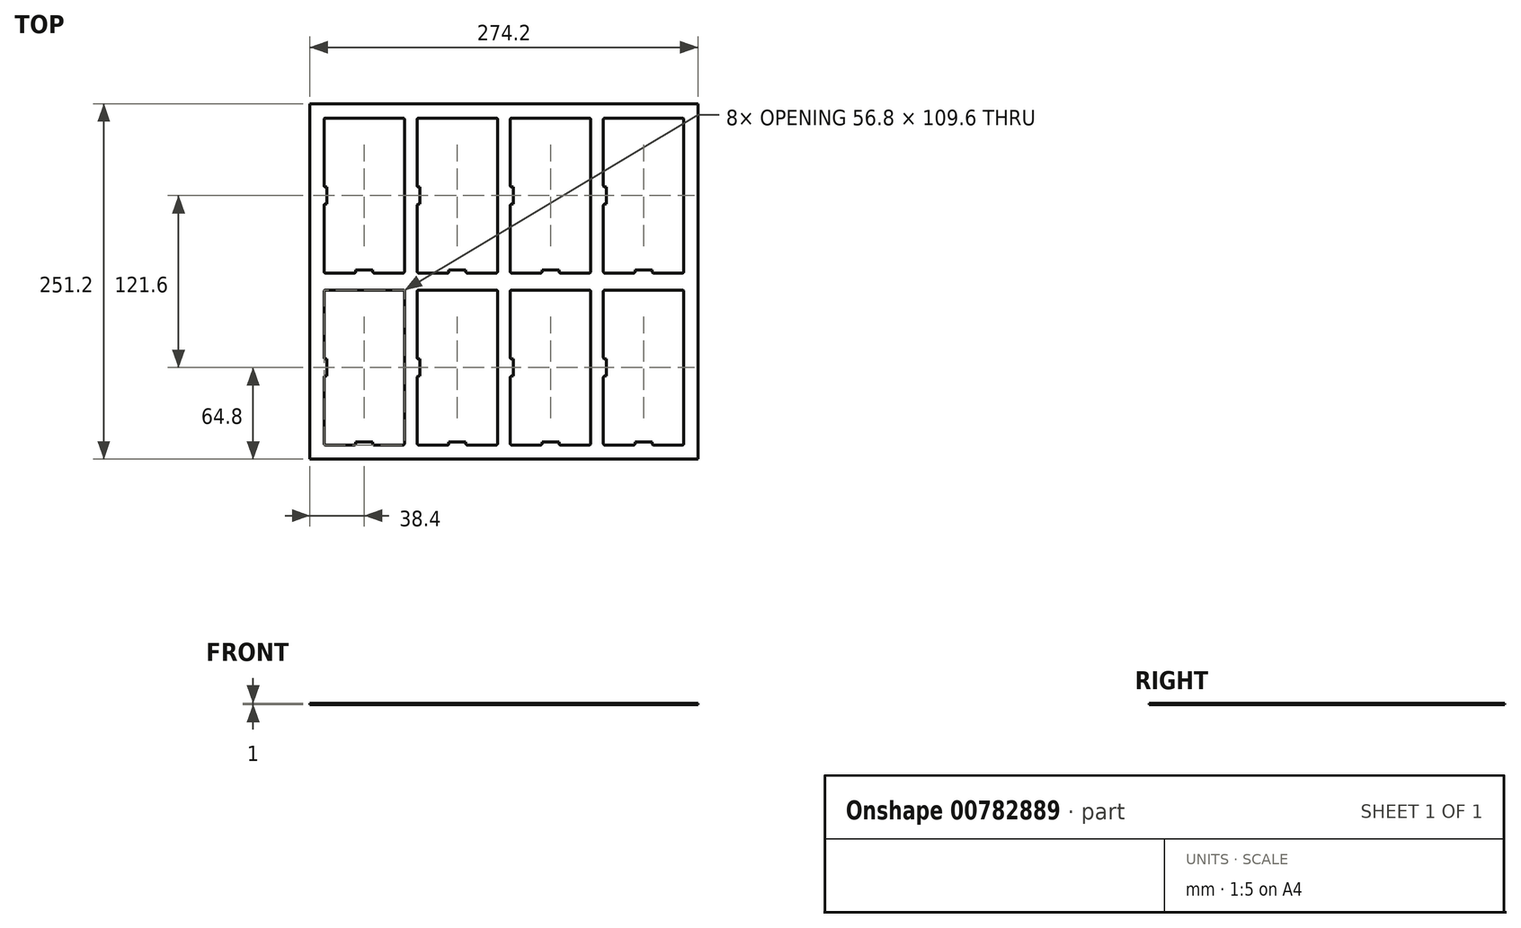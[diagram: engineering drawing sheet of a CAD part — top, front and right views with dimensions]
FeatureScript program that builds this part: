
annotation { "Feature Type Name" : "Feature", "Feature Type Description" : "" }
export const myFeature = defineFeature(function(context is Context, id is Id, definition is map)
    precondition{}
    {
        {
            var Q0;
            Q0=qCreatedBy(makeId("Top.planeOp"),FACE);
            var sketch = newSketch(context, id + "F0", { "sketchPlane" : qUnion([Q0])});
            skLineSegment(sketch, "E0.bottom", {"start": v(137.1, -125.6) * mm, "end": v(-137.1, -125.6) * mm});
            skLineSegment(sketch, "E0.top", {"start": v(137.1, 125.6) * mm, "end": v(-137.1, 125.6) * mm});
            skLineSegment(sketch, "E0.left", {"start": v(137.1, -125.6) * mm, "end": v(137.1, 125.6) * mm});
            skLineSegment(sketch, "E0.right", {"start": v(-137.1, -125.6) * mm, "end": v(-137.1, 125.6) * mm});
            skPoint(sketch, "E0.middle", {"position": v(0, 0) * mm});
            skSolve(sketch);
        }
        {
            var Q0;
            Q0 = qSketchRegion(id + "F0", true);
            extrude(context, id + "F1", {"entities" : qUnion([Q0]), "depth" : 1 * mm, "offsetDistance" : 25 * mm});
        }
        {
            var Q0;
            Q0=makeQuery(id+"F1.opExtrude","CAP_FACE",FACE,{"disambiguationData":[OSD([sQuery(id+"F0.wireOp",EDGE,"E0.bottom"),sQuery(id+"F0.wireOp",EDGE,"E0.top"),sQuery(id+"F0.wireOp",EDGE,"E0.left"),sQuery(id+"F0.wireOp",EDGE,"E0.right")])],"isStart":false});
            var sketch = newSketch(context, id + "F2", { "sketchPlane" : qUnion([Q0])});
            skLineSegment(sketch, "E1.bottom", {"start": v(-125.1, -10) * mm, "end": v(-74.3, -10) * mm, "construction": true});
            skLineSegment(sketch, "E1.top", {"start": v(-125.1, -113.6) * mm, "end": v(-74.3, -113.6) * mm, "construction": true});
            skLineSegment(sketch, "E1.left", {"start": v(-125.1, -10) * mm, "end": v(-125.1, -113.6) * mm, "construction": true});
            skLineSegment(sketch, "E1.right", {"start": v(-74.3, -10) * mm, "end": v(-74.3, -113.6) * mm, "construction": true});
            skLineSegment(sketch, "E2.bottom", {"start": v(-127.1, -115.6) * mm, "end": v(-70.3, -115.6) * mm});
            skLineSegment(sketch, "E2.top", {"start": v(-127.1, -6) * mm, "end": v(-70.3, -6) * mm});
            skLineSegment(sketch, "E2.left", {"start": v(-127.1, -115.6) * mm, "end": v(-127.1, -6) * mm});
            skLineSegment(sketch, "E2.right", {"start": v(-70.3, -115.6) * mm, "end": v(-70.3, -6) * mm});
            skLineSegment(sketch, "E3.top", {"start": v(-92.7, -113.6) * mm, "end": v(-104.7, -113.6) * mm});
            skLineSegment(sketch, "E3.left", {"start": v(-92.7, -115.6) * mm, "end": v(-92.7, -113.6) * mm});
            skLineSegment(sketch, "E3.right", {"start": v(-104.7, -115.6) * mm, "end": v(-104.7, -113.6) * mm});
            skPoint(sketch, "E3.middle", {"position": v(-98.7, -115.6) * mm});
            skPoint(sketch, "E4.orphan", {"position": v(-104.7, -117.6) * mm});
            skPoint(sketch, "E5.orphan", {"position": v(-92.7, -117.6) * mm});
            skLineSegment(sketch, "E6.bottom", {"start": v(-125.1, -66.8) * mm, "end": v(-127.1, -66.8) * mm});
            skLineSegment(sketch, "E6.top", {"start": v(-125.1, -54.8) * mm, "end": v(-127.1, -54.8) * mm});
            skLineSegment(sketch, "E6.left", {"start": v(-125.1, -66.8) * mm, "end": v(-125.1, -54.8) * mm});
            skPoint(sketch, "E6.middle", {"position": v(-127.1, -60.8) * mm});
            skPoint(sketch, "E7.orphan", {"position": v(-129.1, -54.8) * mm});
            skPoint(sketch, "E8.orphan", {"position": v(-129.1, -66.8) * mm});
            skLineSegment(sketch, "E9.0.1.0", {"start": v(-127.1, 115.6) * mm, "end": v(-70.3, 115.6) * mm});
            skLineSegment(sketch, "E9.0.1.1", {"start": v(-70.3, 6) * mm, "end": v(-70.3, 115.6) * mm});
            skLineSegment(sketch, "E9.0.1.2", {"start": v(-127.1, 6) * mm, "end": v(-70.3, 6) * mm});
            skLineSegment(sketch, "E9.0.1.3", {"start": v(-127.1, 6) * mm, "end": v(-127.1, 115.6) * mm});
            skLineSegment(sketch, "E9.0.1.4", {"start": v(-104.7, 6) * mm, "end": v(-104.7, 8) * mm});
            skLineSegment(sketch, "E9.0.1.5", {"start": v(-92.7, 6) * mm, "end": v(-92.7, 8) * mm});
            skLineSegment(sketch, "E9.0.1.6", {"start": v(-92.7, 8) * mm, "end": v(-104.7, 8) * mm});
            skLineSegment(sketch, "E9.0.1.7", {"start": v(-125.1, 66.8) * mm, "end": v(-127.1, 66.8) * mm});
            skLineSegment(sketch, "E9.0.1.8", {"start": v(-125.1, 54.8) * mm, "end": v(-127.1, 54.8) * mm});
            skLineSegment(sketch, "E9.0.1.9", {"start": v(-125.1, 54.8) * mm, "end": v(-125.1, 66.8) * mm});
            skLineSegment(sketch, "E9.1.0.0", {"start": v(-61.3, -6) * mm, "end": v(-4.5, -6) * mm});
            skLineSegment(sketch, "E9.1.0.1", {"start": v(-4.5, -115.6) * mm, "end": v(-4.5, -6) * mm});
            skLineSegment(sketch, "E9.1.0.2", {"start": v(-61.3, -115.6) * mm, "end": v(-4.5, -115.6) * mm});
            skLineSegment(sketch, "E9.1.0.3", {"start": v(-61.3, -115.6) * mm, "end": v(-61.3, -6) * mm});
            skLineSegment(sketch, "E9.1.0.4", {"start": v(-38.9, -115.6) * mm, "end": v(-38.9, -113.6) * mm});
            skLineSegment(sketch, "E9.1.0.5", {"start": v(-26.9, -115.6) * mm, "end": v(-26.9, -113.6) * mm});
            skLineSegment(sketch, "E9.1.0.6", {"start": v(-26.9, -113.6) * mm, "end": v(-38.9, -113.6) * mm});
            skLineSegment(sketch, "E9.1.0.7", {"start": v(-59.3, -54.8) * mm, "end": v(-61.3, -54.8) * mm});
            skLineSegment(sketch, "E9.1.0.8", {"start": v(-59.3, -66.8) * mm, "end": v(-61.3, -66.8) * mm});
            skLineSegment(sketch, "E9.1.0.9", {"start": v(-59.3, -66.8) * mm, "end": v(-59.3, -54.8) * mm});
            skLineSegment(sketch, "E9.1.1.0", {"start": v(-61.3, 115.6) * mm, "end": v(-4.5, 115.6) * mm});
            skLineSegment(sketch, "E9.1.1.1", {"start": v(-4.5, 6) * mm, "end": v(-4.5, 115.6) * mm});
            skLineSegment(sketch, "E9.1.1.2", {"start": v(-61.3, 6) * mm, "end": v(-4.5, 6) * mm});
            skLineSegment(sketch, "E9.1.1.3", {"start": v(-61.3, 6) * mm, "end": v(-61.3, 115.6) * mm});
            skLineSegment(sketch, "E9.1.1.4", {"start": v(-38.9, 6) * mm, "end": v(-38.9, 8) * mm});
            skLineSegment(sketch, "E9.1.1.5", {"start": v(-26.9, 6) * mm, "end": v(-26.9, 8) * mm});
            skLineSegment(sketch, "E9.1.1.6", {"start": v(-26.9, 8) * mm, "end": v(-38.9, 8) * mm});
            skLineSegment(sketch, "E9.1.1.7", {"start": v(-59.3, 66.8) * mm, "end": v(-61.3, 66.8) * mm});
            skLineSegment(sketch, "E9.1.1.8", {"start": v(-59.3, 54.8) * mm, "end": v(-61.3, 54.8) * mm});
            skLineSegment(sketch, "E9.1.1.9", {"start": v(-59.3, 54.8) * mm, "end": v(-59.3, 66.8) * mm});
            skLineSegment(sketch, "E9.2.0.0", {"start": v(4.5, -6) * mm, "end": v(61.3, -6) * mm});
            skLineSegment(sketch, "E9.2.0.1", {"start": v(61.3, -115.6) * mm, "end": v(61.3, -6) * mm});
            skLineSegment(sketch, "E9.2.0.2", {"start": v(4.5, -115.6) * mm, "end": v(61.3, -115.6) * mm});
            skLineSegment(sketch, "E9.2.0.3", {"start": v(4.5, -115.6) * mm, "end": v(4.5, -6) * mm});
            skLineSegment(sketch, "E9.2.0.4", {"start": v(26.9, -115.6) * mm, "end": v(26.9, -113.6) * mm});
            skLineSegment(sketch, "E9.2.0.5", {"start": v(38.9, -115.6) * mm, "end": v(38.9, -113.6) * mm});
            skLineSegment(sketch, "E9.2.0.6", {"start": v(38.9, -113.6) * mm, "end": v(26.9, -113.6) * mm});
            skLineSegment(sketch, "E9.2.0.7", {"start": v(6.5, -54.8) * mm, "end": v(4.5, -54.8) * mm});
            skLineSegment(sketch, "E9.2.0.8", {"start": v(6.5, -66.8) * mm, "end": v(4.5, -66.8) * mm});
            skLineSegment(sketch, "E9.2.0.9", {"start": v(6.5, -66.8) * mm, "end": v(6.5, -54.8) * mm});
            skLineSegment(sketch, "E9.2.1.0", {"start": v(4.5, 115.6) * mm, "end": v(61.3, 115.6) * mm});
            skLineSegment(sketch, "E9.2.1.1", {"start": v(61.3, 6) * mm, "end": v(61.3, 115.6) * mm});
            skLineSegment(sketch, "E9.2.1.2", {"start": v(4.5, 6) * mm, "end": v(61.3, 6) * mm});
            skLineSegment(sketch, "E9.2.1.3", {"start": v(4.5, 6) * mm, "end": v(4.5, 115.6) * mm});
            skLineSegment(sketch, "E9.2.1.4", {"start": v(26.9, 6) * mm, "end": v(26.9, 8) * mm});
            skLineSegment(sketch, "E9.2.1.5", {"start": v(38.9, 6) * mm, "end": v(38.9, 8) * mm});
            skLineSegment(sketch, "E9.2.1.6", {"start": v(38.9, 8) * mm, "end": v(26.9, 8) * mm});
            skLineSegment(sketch, "E9.2.1.7", {"start": v(6.5, 66.8) * mm, "end": v(4.5, 66.8) * mm});
            skLineSegment(sketch, "E9.2.1.8", {"start": v(6.5, 54.8) * mm, "end": v(4.5, 54.8) * mm});
            skLineSegment(sketch, "E9.2.1.9", {"start": v(6.5, 54.8) * mm, "end": v(6.5, 66.8) * mm});
            skLineSegment(sketch, "E9.3.0.0", {"start": v(70.3, -6) * mm, "end": v(127.1, -6) * mm});
            skLineSegment(sketch, "E9.3.0.1", {"start": v(127.1, -115.6) * mm, "end": v(127.1, -6) * mm});
            skLineSegment(sketch, "E9.3.0.2", {"start": v(70.3, -115.6) * mm, "end": v(127.1, -115.6) * mm});
            skLineSegment(sketch, "E9.3.0.3", {"start": v(70.3, -115.6) * mm, "end": v(70.3, -6) * mm});
            skLineSegment(sketch, "E9.3.0.4", {"start": v(92.7, -115.6) * mm, "end": v(92.7, -113.6) * mm});
            skLineSegment(sketch, "E9.3.0.5", {"start": v(104.7, -115.6) * mm, "end": v(104.7, -113.6) * mm});
            skLineSegment(sketch, "E9.3.0.6", {"start": v(104.7, -113.6) * mm, "end": v(92.7, -113.6) * mm});
            skLineSegment(sketch, "E9.3.0.7", {"start": v(72.3, -54.8) * mm, "end": v(70.3, -54.8) * mm});
            skLineSegment(sketch, "E9.3.0.8", {"start": v(72.3, -66.8) * mm, "end": v(70.3, -66.8) * mm});
            skLineSegment(sketch, "E9.3.0.9", {"start": v(72.3, -66.8) * mm, "end": v(72.3, -54.8) * mm});
            skLineSegment(sketch, "E9.3.1.0", {"start": v(70.3, 115.6) * mm, "end": v(127.1, 115.6) * mm});
            skLineSegment(sketch, "E9.3.1.1", {"start": v(127.1, 6) * mm, "end": v(127.1, 115.6) * mm});
            skLineSegment(sketch, "E9.3.1.2", {"start": v(70.3, 6) * mm, "end": v(127.1, 6) * mm});
            skLineSegment(sketch, "E9.3.1.3", {"start": v(70.3, 6) * mm, "end": v(70.3, 115.6) * mm});
            skLineSegment(sketch, "E9.3.1.4", {"start": v(92.7, 6) * mm, "end": v(92.7, 8) * mm});
            skLineSegment(sketch, "E9.3.1.5", {"start": v(104.7, 6) * mm, "end": v(104.7, 8) * mm});
            skLineSegment(sketch, "E9.3.1.6", {"start": v(104.7, 8) * mm, "end": v(92.7, 8) * mm});
            skLineSegment(sketch, "E9.3.1.7", {"start": v(72.3, 66.8) * mm, "end": v(70.3, 66.8) * mm});
            skLineSegment(sketch, "E9.3.1.8", {"start": v(72.3, 54.8) * mm, "end": v(70.3, 54.8) * mm});
            skLineSegment(sketch, "E9.3.1.9", {"start": v(72.3, 54.8) * mm, "end": v(72.3, 66.8) * mm});
            skLineSegment(sketch, "E9.direction1", {"start": v(-127.1, -115.6) * mm, "end": v(-61.3, -115.6) * mm, "construction": true});
            skLineSegment(sketch, "E9.direction2", {"start": v(-127.1, -115.6) * mm, "end": v(-127.1, 6) * mm, "construction": true});
            skSolve(sketch);
        }
        {
            var Q0;
            {var subQ4=sQuery(id+"F2.wireOp",EDGE,"E2.top");Q0=makeQuery(id+"F2.imprint","IMPRINT",FACE,{"disambiguationData":[TD([[makeQuery(id+"F2.imprint","IMPRINT",EDGE,{"derivedFrom":subQ4}),-1.0]])]});}
            var Q1;
            {var subQ3=sQuery(id+"F2.wireOp",EDGE,"E9.1.0.0");Q1=makeQuery(id+"F2.imprint","IMPRINT",FACE,{"disambiguationData":[TD([[makeQuery(id+"F2.imprint","IMPRINT",EDGE,{"derivedFrom":subQ3}),-1.0]])]});}
            var Q2;
            {var subQ3=sQuery(id+"F2.wireOp",EDGE,"E9.2.0.0");Q2=makeQuery(id+"F2.imprint","IMPRINT",FACE,{"disambiguationData":[TD([[makeQuery(id+"F2.imprint","IMPRINT",EDGE,{"derivedFrom":subQ3}),-1.0]])]});}
            var Q3;
            {var subQ3=sQuery(id+"F2.wireOp",EDGE,"E9.3.0.0");Q3=makeQuery(id+"F2.imprint","IMPRINT",FACE,{"disambiguationData":[TD([[makeQuery(id+"F2.imprint","IMPRINT",EDGE,{"derivedFrom":subQ3}),-1.0]])]});}
            var Q4;
            {var subQ3=sQuery(id+"F2.wireOp",EDGE,"E9.3.1.0");Q4=makeQuery(id+"F2.imprint","IMPRINT",FACE,{"disambiguationData":[TD([[makeQuery(id+"F2.imprint","IMPRINT",EDGE,{"derivedFrom":subQ3}),-1.0]])]});}
            var Q5;
            {var subQ3=sQuery(id+"F2.wireOp",EDGE,"E9.2.1.0");Q5=makeQuery(id+"F2.imprint","IMPRINT",FACE,{"disambiguationData":[TD([[makeQuery(id+"F2.imprint","IMPRINT",EDGE,{"derivedFrom":subQ3}),-1.0]])]});}
            var Q6;
            {var subQ3=sQuery(id+"F2.wireOp",EDGE,"E9.1.1.0");Q6=makeQuery(id+"F2.imprint","IMPRINT",FACE,{"disambiguationData":[TD([[makeQuery(id+"F2.imprint","IMPRINT",EDGE,{"derivedFrom":subQ3}),-1.0]])]});}
            var Q7;
            {var subQ3=sQuery(id+"F2.wireOp",EDGE,"E9.0.1.0");Q7=makeQuery(id+"F2.imprint","IMPRINT",FACE,{"disambiguationData":[TD([[makeQuery(id+"F2.imprint","IMPRINT",EDGE,{"derivedFrom":subQ3}),-1.0]])]});}
            extrude(context, id + "F3", {"entities" : qUnion([Q0, Q1, Q2, Q3, Q4, Q5, Q6, Q7]), "operationType" : NewBodyOperationType.REMOVE, "endBound" : BoundingType.THROUGH_ALL, "oppositeDirection" : true, "depth" : 25 * mm, "offsetDistance" : 25 * mm});
        }
        {
            var Q0;
            Q0=makeQuery(id+"F3.boolean.opBoolean","COPY",EDGE,{"derivedFrom":makeQuery(id+"F3.opExtrude","SWEPT_EDGE",EDGE,{"disambiguationData":[OSD([sQuery(id+"F2.wireOp",EDGE,"E2.bottom"),sQuery(id+"F2.wireOp",EDGE,"E2.left")])]})});
            var Q1;
            Q1=makeQuery(id+"F3.boolean.opBoolean","COPY",EDGE,{"derivedFrom":makeQuery(id+"F3.opExtrude","SWEPT_EDGE",EDGE,{"disambiguationData":[OSD([sQuery(id+"F2.wireOp",EDGE,"E2.bottom"),sQuery(id+"F2.wireOp",EDGE,"E3.right")])]})});
            var Q2;
            Q2=makeQuery(id+"F3.boolean.opBoolean","COPY",EDGE,{"derivedFrom":makeQuery(id+"F3.opExtrude","SWEPT_EDGE",EDGE,{"disambiguationData":[OSD([sQuery(id+"F2.wireOp",EDGE,"E2.bottom"),sQuery(id+"F2.wireOp",EDGE,"E3.left")])]})});
            var Q3;
            Q3=makeQuery(id+"F3.boolean.opBoolean","COPY",EDGE,{"derivedFrom":makeQuery(id+"F3.opExtrude","SWEPT_EDGE",EDGE,{"disambiguationData":[OSD([sQuery(id+"F2.wireOp",EDGE,"E2.bottom"),sQuery(id+"F2.wireOp",EDGE,"E2.right")])]})});
            var Q4;
            Q4=makeQuery(id+"F3.boolean.opBoolean","COPY",EDGE,{"derivedFrom":makeQuery(id+"F3.opExtrude","SWEPT_EDGE",EDGE,{"disambiguationData":[OSD([sQuery(id+"F2.wireOp",EDGE,"E2.top"),sQuery(id+"F2.wireOp",EDGE,"E2.right")])]})});
            var Q5;
            Q5=makeQuery(id+"F3.boolean.opBoolean","COPY",EDGE,{"derivedFrom":makeQuery(id+"F3.opExtrude","SWEPT_EDGE",EDGE,{"disambiguationData":[OSD([sQuery(id+"F2.wireOp",EDGE,"E2.top"),sQuery(id+"F2.wireOp",EDGE,"E2.left")])]})});
            var Q6;
            Q6=makeQuery(id+"F3.boolean.opBoolean","COPY",EDGE,{"derivedFrom":makeQuery(id+"F3.opExtrude","SWEPT_EDGE",EDGE,{"disambiguationData":[OSD([sQuery(id+"F2.wireOp",EDGE,"E2.left"),sQuery(id+"F2.wireOp",EDGE,"E6.top")])]})});
            var Q7;
            Q7=makeQuery(id+"F3.boolean.opBoolean","COPY",EDGE,{"derivedFrom":makeQuery(id+"F3.opExtrude","SWEPT_EDGE",EDGE,{"disambiguationData":[OSD([sQuery(id+"F2.wireOp",EDGE,"E2.left"),sQuery(id+"F2.wireOp",EDGE,"E6.bottom")])]})});
            var Q8;
            Q8=makeQuery(id+"F3.boolean.opBoolean","COPY",EDGE,{"derivedFrom":makeQuery(id+"F3.opExtrude","SWEPT_EDGE",EDGE,{"disambiguationData":[OSD([sQuery(id+"F2.wireOp",EDGE,"E9.1.0.0"),sQuery(id+"F2.wireOp",EDGE,"E9.1.0.3")])]})});
            var Q9;
            Q9=makeQuery(id+"F3.boolean.opBoolean","COPY",EDGE,{"derivedFrom":makeQuery(id+"F3.opExtrude","SWEPT_EDGE",EDGE,{"disambiguationData":[OSD([sQuery(id+"F2.wireOp",EDGE,"E9.1.0.0"),sQuery(id+"F2.wireOp",EDGE,"E9.1.0.1")])]})});
            var Q10;
            Q10=makeQuery(id+"F3.boolean.opBoolean","COPY",EDGE,{"derivedFrom":makeQuery(id+"F3.opExtrude","SWEPT_EDGE",EDGE,{"disambiguationData":[OSD([sQuery(id+"F2.wireOp",EDGE,"E9.1.0.3"),sQuery(id+"F2.wireOp",EDGE,"E9.1.0.7")])]})});
            var Q11;
            Q11=makeQuery(id+"F3.boolean.opBoolean","COPY",EDGE,{"derivedFrom":makeQuery(id+"F3.opExtrude","SWEPT_EDGE",EDGE,{"disambiguationData":[OSD([sQuery(id+"F2.wireOp",EDGE,"E9.1.0.3"),sQuery(id+"F2.wireOp",EDGE,"E9.1.0.8")])]})});
            var Q12;
            Q12=makeQuery(id+"F3.boolean.opBoolean","COPY",EDGE,{"derivedFrom":makeQuery(id+"F3.opExtrude","SWEPT_EDGE",EDGE,{"disambiguationData":[OSD([sQuery(id+"F2.wireOp",EDGE,"E9.1.0.2"),sQuery(id+"F2.wireOp",EDGE,"E9.1.0.3")])]})});
            var Q13;
            Q13=makeQuery(id+"F3.boolean.opBoolean","COPY",EDGE,{"derivedFrom":makeQuery(id+"F3.opExtrude","SWEPT_EDGE",EDGE,{"disambiguationData":[OSD([sQuery(id+"F2.wireOp",EDGE,"E9.1.0.2"),sQuery(id+"F2.wireOp",EDGE,"E9.1.0.4")])]})});
            var Q14;
            Q14=makeQuery(id+"F3.boolean.opBoolean","COPY",EDGE,{"derivedFrom":makeQuery(id+"F3.opExtrude","SWEPT_EDGE",EDGE,{"disambiguationData":[OSD([sQuery(id+"F2.wireOp",EDGE,"E9.1.0.2"),sQuery(id+"F2.wireOp",EDGE,"E9.1.0.5")])]})});
            var Q15;
            Q15=makeQuery(id+"F3.boolean.opBoolean","COPY",EDGE,{"derivedFrom":makeQuery(id+"F3.opExtrude","SWEPT_EDGE",EDGE,{"disambiguationData":[OSD([sQuery(id+"F2.wireOp",EDGE,"E9.1.0.1"),sQuery(id+"F2.wireOp",EDGE,"E9.1.0.2")])]})});
            var Q16;
            Q16=makeQuery(id+"F3.boolean.opBoolean","COPY",EDGE,{"derivedFrom":makeQuery(id+"F3.opExtrude","SWEPT_EDGE",EDGE,{"disambiguationData":[OSD([sQuery(id+"F2.wireOp",EDGE,"E9.2.0.2"),sQuery(id+"F2.wireOp",EDGE,"E9.2.0.3")])]})});
            var Q17;
            Q17=makeQuery(id+"F3.boolean.opBoolean","COPY",EDGE,{"derivedFrom":makeQuery(id+"F3.opExtrude","SWEPT_EDGE",EDGE,{"disambiguationData":[OSD([sQuery(id+"F2.wireOp",EDGE,"E9.2.0.2"),sQuery(id+"F2.wireOp",EDGE,"E9.2.0.4")])]})});
            var Q18;
            Q18=makeQuery(id+"F3.boolean.opBoolean","COPY",EDGE,{"derivedFrom":makeQuery(id+"F3.opExtrude","SWEPT_EDGE",EDGE,{"disambiguationData":[OSD([sQuery(id+"F2.wireOp",EDGE,"E9.2.0.2"),sQuery(id+"F2.wireOp",EDGE,"E9.2.0.5")])]})});
            var Q19;
            Q19=makeQuery(id+"F3.boolean.opBoolean","COPY",EDGE,{"derivedFrom":makeQuery(id+"F3.opExtrude","SWEPT_EDGE",EDGE,{"disambiguationData":[OSD([sQuery(id+"F2.wireOp",EDGE,"E9.2.0.1"),sQuery(id+"F2.wireOp",EDGE,"E9.2.0.2")])]})});
            var Q20;
            Q20=makeQuery(id+"F3.boolean.opBoolean","COPY",EDGE,{"derivedFrom":makeQuery(id+"F3.opExtrude","SWEPT_EDGE",EDGE,{"disambiguationData":[OSD([sQuery(id+"F2.wireOp",EDGE,"E9.2.0.0"),sQuery(id+"F2.wireOp",EDGE,"E9.2.0.1")])]})});
            var Q21;
            Q21=makeQuery(id+"F3.boolean.opBoolean","COPY",EDGE,{"derivedFrom":makeQuery(id+"F3.opExtrude","SWEPT_EDGE",EDGE,{"disambiguationData":[OSD([sQuery(id+"F2.wireOp",EDGE,"E9.2.0.0"),sQuery(id+"F2.wireOp",EDGE,"E9.2.0.3")])]})});
            var Q22;
            Q22=makeQuery(id+"F3.boolean.opBoolean","COPY",EDGE,{"derivedFrom":makeQuery(id+"F3.opExtrude","SWEPT_EDGE",EDGE,{"disambiguationData":[OSD([sQuery(id+"F2.wireOp",EDGE,"E9.2.0.3"),sQuery(id+"F2.wireOp",EDGE,"E9.2.0.7")])]})});
            var Q23;
            Q23=makeQuery(id+"F3.boolean.opBoolean","COPY",EDGE,{"derivedFrom":makeQuery(id+"F3.opExtrude","SWEPT_EDGE",EDGE,{"disambiguationData":[OSD([sQuery(id+"F2.wireOp",EDGE,"E9.2.0.3"),sQuery(id+"F2.wireOp",EDGE,"E9.2.0.8")])]})});
            var Q24;
            Q24=makeQuery(id+"F3.boolean.opBoolean","COPY",EDGE,{"derivedFrom":makeQuery(id+"F3.opExtrude","SWEPT_EDGE",EDGE,{"disambiguationData":[OSD([sQuery(id+"F2.wireOp",EDGE,"E9.3.0.0"),sQuery(id+"F2.wireOp",EDGE,"E9.3.0.3")])]})});
            var Q25;
            Q25=makeQuery(id+"F3.boolean.opBoolean","COPY",EDGE,{"derivedFrom":makeQuery(id+"F3.opExtrude","SWEPT_EDGE",EDGE,{"disambiguationData":[OSD([sQuery(id+"F2.wireOp",EDGE,"E9.3.0.3"),sQuery(id+"F2.wireOp",EDGE,"E9.3.0.7")])]})});
            var Q26;
            Q26=makeQuery(id+"F3.boolean.opBoolean","COPY",EDGE,{"derivedFrom":makeQuery(id+"F3.opExtrude","SWEPT_EDGE",EDGE,{"disambiguationData":[OSD([sQuery(id+"F2.wireOp",EDGE,"E9.3.0.3"),sQuery(id+"F2.wireOp",EDGE,"E9.3.0.8")])]})});
            var Q27;
            Q27=makeQuery(id+"F3.boolean.opBoolean","COPY",EDGE,{"derivedFrom":makeQuery(id+"F3.opExtrude","SWEPT_EDGE",EDGE,{"disambiguationData":[OSD([sQuery(id+"F2.wireOp",EDGE,"E9.3.0.2"),sQuery(id+"F2.wireOp",EDGE,"E9.3.0.3")])]})});
            var Q28;
            Q28=makeQuery(id+"F3.boolean.opBoolean","COPY",EDGE,{"derivedFrom":makeQuery(id+"F3.opExtrude","SWEPT_EDGE",EDGE,{"disambiguationData":[OSD([sQuery(id+"F2.wireOp",EDGE,"E9.3.0.2"),sQuery(id+"F2.wireOp",EDGE,"E9.3.0.4")])]})});
            var Q29;
            Q29=makeQuery(id+"F3.boolean.opBoolean","COPY",EDGE,{"derivedFrom":makeQuery(id+"F3.opExtrude","SWEPT_EDGE",EDGE,{"disambiguationData":[OSD([sQuery(id+"F2.wireOp",EDGE,"E9.3.0.2"),sQuery(id+"F2.wireOp",EDGE,"E9.3.0.5")])]})});
            var Q30;
            Q30=makeQuery(id+"F3.boolean.opBoolean","COPY",EDGE,{"derivedFrom":makeQuery(id+"F3.opExtrude","SWEPT_EDGE",EDGE,{"disambiguationData":[OSD([sQuery(id+"F2.wireOp",EDGE,"E9.3.0.1"),sQuery(id+"F2.wireOp",EDGE,"E9.3.0.2")])]})});
            var Q31;
            Q31=makeQuery(id+"F3.boolean.opBoolean","COPY",EDGE,{"derivedFrom":makeQuery(id+"F3.opExtrude","SWEPT_EDGE",EDGE,{"disambiguationData":[OSD([sQuery(id+"F2.wireOp",EDGE,"E9.3.0.0"),sQuery(id+"F2.wireOp",EDGE,"E9.3.0.1")])]})});
            var Q32;
            Q32=makeQuery(id+"F3.boolean.opBoolean","COPY",EDGE,{"derivedFrom":makeQuery(id+"F3.opExtrude","SWEPT_EDGE",EDGE,{"disambiguationData":[OSD([sQuery(id+"F2.wireOp",EDGE,"E9.0.1.2"),sQuery(id+"F2.wireOp",EDGE,"E9.0.1.3")])]})});
            var Q33;
            Q33=makeQuery(id+"F3.boolean.opBoolean","COPY",EDGE,{"derivedFrom":makeQuery(id+"F3.opExtrude","SWEPT_EDGE",EDGE,{"disambiguationData":[OSD([sQuery(id+"F2.wireOp",EDGE,"E9.0.1.2"),sQuery(id+"F2.wireOp",EDGE,"E9.0.1.4")])]})});
            var Q34;
            Q34=makeQuery(id+"F3.boolean.opBoolean","COPY",EDGE,{"derivedFrom":makeQuery(id+"F3.opExtrude","SWEPT_EDGE",EDGE,{"disambiguationData":[OSD([sQuery(id+"F2.wireOp",EDGE,"E9.0.1.2"),sQuery(id+"F2.wireOp",EDGE,"E9.0.1.5")])]})});
            var Q35;
            Q35=makeQuery(id+"F3.boolean.opBoolean","COPY",EDGE,{"derivedFrom":makeQuery(id+"F3.opExtrude","SWEPT_EDGE",EDGE,{"disambiguationData":[OSD([sQuery(id+"F2.wireOp",EDGE,"E9.0.1.1"),sQuery(id+"F2.wireOp",EDGE,"E9.0.1.2")])]})});
            var Q36;
            Q36=makeQuery(id+"F3.boolean.opBoolean","COPY",EDGE,{"derivedFrom":makeQuery(id+"F3.opExtrude","SWEPT_EDGE",EDGE,{"disambiguationData":[OSD([sQuery(id+"F2.wireOp",EDGE,"E9.0.1.0"),sQuery(id+"F2.wireOp",EDGE,"E9.0.1.1")])]})});
            var Q37;
            Q37=makeQuery(id+"F3.boolean.opBoolean","COPY",EDGE,{"derivedFrom":makeQuery(id+"F3.opExtrude","SWEPT_EDGE",EDGE,{"disambiguationData":[OSD([sQuery(id+"F2.wireOp",EDGE,"E9.0.1.0"),sQuery(id+"F2.wireOp",EDGE,"E9.0.1.3")])]})});
            var Q38;
            Q38=makeQuery(id+"F3.boolean.opBoolean","COPY",EDGE,{"derivedFrom":makeQuery(id+"F3.opExtrude","SWEPT_EDGE",EDGE,{"disambiguationData":[OSD([sQuery(id+"F2.wireOp",EDGE,"E9.0.1.3"),sQuery(id+"F2.wireOp",EDGE,"E9.0.1.7")])]})});
            var Q39;
            Q39=makeQuery(id+"F3.boolean.opBoolean","COPY",EDGE,{"derivedFrom":makeQuery(id+"F3.opExtrude","SWEPT_EDGE",EDGE,{"disambiguationData":[OSD([sQuery(id+"F2.wireOp",EDGE,"E9.0.1.3"),sQuery(id+"F2.wireOp",EDGE,"E9.0.1.8")])]})});
            var Q40;
            Q40=makeQuery(id+"F3.boolean.opBoolean","COPY",EDGE,{"derivedFrom":makeQuery(id+"F3.opExtrude","SWEPT_EDGE",EDGE,{"disambiguationData":[OSD([sQuery(id+"F2.wireOp",EDGE,"E9.1.1.0"),sQuery(id+"F2.wireOp",EDGE,"E9.1.1.3")])]})});
            var Q41;
            Q41=makeQuery(id+"F3.boolean.opBoolean","COPY",EDGE,{"derivedFrom":makeQuery(id+"F3.opExtrude","SWEPT_EDGE",EDGE,{"disambiguationData":[OSD([sQuery(id+"F2.wireOp",EDGE,"E9.1.1.3"),sQuery(id+"F2.wireOp",EDGE,"E9.1.1.7")])]})});
            var Q42;
            Q42=makeQuery(id+"F3.boolean.opBoolean","COPY",EDGE,{"derivedFrom":makeQuery(id+"F3.opExtrude","SWEPT_EDGE",EDGE,{"disambiguationData":[OSD([sQuery(id+"F2.wireOp",EDGE,"E9.1.1.3"),sQuery(id+"F2.wireOp",EDGE,"E9.1.1.8")])]})});
            var Q43;
            Q43=makeQuery(id+"F3.boolean.opBoolean","COPY",EDGE,{"derivedFrom":makeQuery(id+"F3.opExtrude","SWEPT_EDGE",EDGE,{"disambiguationData":[OSD([sQuery(id+"F2.wireOp",EDGE,"E9.1.1.2"),sQuery(id+"F2.wireOp",EDGE,"E9.1.1.3")])]})});
            var Q44;
            Q44=makeQuery(id+"F3.boolean.opBoolean","COPY",EDGE,{"derivedFrom":makeQuery(id+"F3.opExtrude","SWEPT_EDGE",EDGE,{"disambiguationData":[OSD([sQuery(id+"F2.wireOp",EDGE,"E9.1.1.2"),sQuery(id+"F2.wireOp",EDGE,"E9.1.1.4")])]})});
            var Q45;
            Q45=makeQuery(id+"F3.boolean.opBoolean","COPY",EDGE,{"derivedFrom":makeQuery(id+"F3.opExtrude","SWEPT_EDGE",EDGE,{"disambiguationData":[OSD([sQuery(id+"F2.wireOp",EDGE,"E9.1.1.2"),sQuery(id+"F2.wireOp",EDGE,"E9.1.1.5")])]})});
            var Q46;
            Q46=makeQuery(id+"F3.boolean.opBoolean","COPY",EDGE,{"derivedFrom":makeQuery(id+"F3.opExtrude","SWEPT_EDGE",EDGE,{"disambiguationData":[OSD([sQuery(id+"F2.wireOp",EDGE,"E9.1.1.1"),sQuery(id+"F2.wireOp",EDGE,"E9.1.1.2")])]})});
            var Q47;
            Q47=makeQuery(id+"F3.boolean.opBoolean","COPY",EDGE,{"derivedFrom":makeQuery(id+"F3.opExtrude","SWEPT_EDGE",EDGE,{"disambiguationData":[OSD([sQuery(id+"F2.wireOp",EDGE,"E9.1.1.0"),sQuery(id+"F2.wireOp",EDGE,"E9.1.1.1")])]})});
            var Q48;
            Q48=makeQuery(id+"F3.boolean.opBoolean","COPY",EDGE,{"derivedFrom":makeQuery(id+"F3.opExtrude","SWEPT_EDGE",EDGE,{"disambiguationData":[OSD([sQuery(id+"F2.wireOp",EDGE,"E9.2.1.0"),sQuery(id+"F2.wireOp",EDGE,"E9.2.1.3")])]})});
            var Q49;
            Q49=makeQuery(id+"F3.boolean.opBoolean","COPY",EDGE,{"derivedFrom":makeQuery(id+"F3.opExtrude","SWEPT_EDGE",EDGE,{"disambiguationData":[OSD([sQuery(id+"F2.wireOp",EDGE,"E9.2.1.3"),sQuery(id+"F2.wireOp",EDGE,"E9.2.1.7")])]})});
            var Q50;
            Q50=makeQuery(id+"F3.boolean.opBoolean","COPY",EDGE,{"derivedFrom":makeQuery(id+"F3.opExtrude","SWEPT_EDGE",EDGE,{"disambiguationData":[OSD([sQuery(id+"F2.wireOp",EDGE,"E9.2.1.3"),sQuery(id+"F2.wireOp",EDGE,"E9.2.1.8")])]})});
            var Q51;
            Q51=makeQuery(id+"F3.boolean.opBoolean","COPY",EDGE,{"derivedFrom":makeQuery(id+"F3.opExtrude","SWEPT_EDGE",EDGE,{"disambiguationData":[OSD([sQuery(id+"F2.wireOp",EDGE,"E9.2.1.2"),sQuery(id+"F2.wireOp",EDGE,"E9.2.1.3")])]})});
            var Q52;
            Q52=makeQuery(id+"F3.boolean.opBoolean","COPY",EDGE,{"derivedFrom":makeQuery(id+"F3.opExtrude","SWEPT_EDGE",EDGE,{"disambiguationData":[OSD([sQuery(id+"F2.wireOp",EDGE,"E9.2.1.2"),sQuery(id+"F2.wireOp",EDGE,"E9.2.1.4")])]})});
            var Q53;
            Q53=makeQuery(id+"F3.boolean.opBoolean","COPY",EDGE,{"derivedFrom":makeQuery(id+"F3.opExtrude","SWEPT_EDGE",EDGE,{"disambiguationData":[OSD([sQuery(id+"F2.wireOp",EDGE,"E9.2.1.2"),sQuery(id+"F2.wireOp",EDGE,"E9.2.1.5")])]})});
            var Q54;
            Q54=makeQuery(id+"F3.boolean.opBoolean","COPY",EDGE,{"derivedFrom":makeQuery(id+"F3.opExtrude","SWEPT_EDGE",EDGE,{"disambiguationData":[OSD([sQuery(id+"F2.wireOp",EDGE,"E9.2.1.1"),sQuery(id+"F2.wireOp",EDGE,"E9.2.1.2")])]})});
            var Q55;
            Q55=makeQuery(id+"F3.boolean.opBoolean","COPY",EDGE,{"derivedFrom":makeQuery(id+"F3.opExtrude","SWEPT_EDGE",EDGE,{"disambiguationData":[OSD([sQuery(id+"F2.wireOp",EDGE,"E9.2.1.0"),sQuery(id+"F2.wireOp",EDGE,"E9.2.1.1")])]})});
            var Q56;
            Q56=makeQuery(id+"F3.boolean.opBoolean","COPY",EDGE,{"derivedFrom":makeQuery(id+"F3.opExtrude","SWEPT_EDGE",EDGE,{"disambiguationData":[OSD([sQuery(id+"F2.wireOp",EDGE,"E9.3.1.0"),sQuery(id+"F2.wireOp",EDGE,"E9.3.1.3")])]})});
            var Q57;
            Q57=makeQuery(id+"F3.boolean.opBoolean","COPY",EDGE,{"derivedFrom":makeQuery(id+"F3.opExtrude","SWEPT_EDGE",EDGE,{"disambiguationData":[OSD([sQuery(id+"F2.wireOp",EDGE,"E9.3.1.3"),sQuery(id+"F2.wireOp",EDGE,"E9.3.1.7")])]})});
            var Q58;
            Q58=makeQuery(id+"F3.boolean.opBoolean","COPY",EDGE,{"derivedFrom":makeQuery(id+"F3.opExtrude","SWEPT_EDGE",EDGE,{"disambiguationData":[OSD([sQuery(id+"F2.wireOp",EDGE,"E9.3.1.3"),sQuery(id+"F2.wireOp",EDGE,"E9.3.1.8")])]})});
            var Q59;
            Q59=makeQuery(id+"F3.boolean.opBoolean","COPY",EDGE,{"derivedFrom":makeQuery(id+"F3.opExtrude","SWEPT_EDGE",EDGE,{"disambiguationData":[OSD([sQuery(id+"F2.wireOp",EDGE,"E9.3.1.2"),sQuery(id+"F2.wireOp",EDGE,"E9.3.1.3")])]})});
            var Q60;
            Q60=makeQuery(id+"F3.boolean.opBoolean","COPY",EDGE,{"derivedFrom":makeQuery(id+"F3.opExtrude","SWEPT_EDGE",EDGE,{"disambiguationData":[OSD([sQuery(id+"F2.wireOp",EDGE,"E9.3.1.2"),sQuery(id+"F2.wireOp",EDGE,"E9.3.1.4")])]})});
            var Q61;
            Q61=makeQuery(id+"F3.boolean.opBoolean","COPY",EDGE,{"derivedFrom":makeQuery(id+"F3.opExtrude","SWEPT_EDGE",EDGE,{"disambiguationData":[OSD([sQuery(id+"F2.wireOp",EDGE,"E9.3.1.2"),sQuery(id+"F2.wireOp",EDGE,"E9.3.1.5")])]})});
            var Q62;
            Q62=makeQuery(id+"F3.boolean.opBoolean","COPY",EDGE,{"derivedFrom":makeQuery(id+"F3.opExtrude","SWEPT_EDGE",EDGE,{"disambiguationData":[OSD([sQuery(id+"F2.wireOp",EDGE,"E9.3.1.1"),sQuery(id+"F2.wireOp",EDGE,"E9.3.1.2")])]})});
            var Q63;
            Q63=makeQuery(id+"F3.boolean.opBoolean","COPY",EDGE,{"derivedFrom":makeQuery(id+"F3.opExtrude","SWEPT_EDGE",EDGE,{"disambiguationData":[OSD([sQuery(id+"F2.wireOp",EDGE,"E9.3.1.0"),sQuery(id+"F2.wireOp",EDGE,"E9.3.1.1")])]})});
            fillet(context, id + "F4", {"entities" : qUnion([Q0, Q1, Q2, Q3, Q4, Q5, Q6, Q7, Q8, Q9, Q10, Q11, Q12, Q13, Q14, Q15, Q16, Q17, Q18, Q19, Q20, Q21, Q22, Q23, Q24, Q25, Q26, Q27, Q28, Q29, Q30, Q31, Q32, Q33, Q34, Q35, Q36, Q37, Q38, Q39, Q40, Q41, Q42, Q43, Q44, Q45, Q46, Q47, Q48, Q49, Q50, Q51, Q52, Q53, Q54, Q55, Q56, Q57, Q58, Q59, Q60, Q61, Q62, Q63]), "radius" : 1 * mm, "tangentPropagation" : true, "allowEdgeOverflow" : false});
        }
    });
